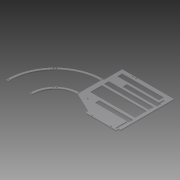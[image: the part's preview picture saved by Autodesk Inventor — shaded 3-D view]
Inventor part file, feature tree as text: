
AUTODESK INVENTOR PART (.ipt)
format: ipt  version: 2013 (Build 170138000, 138)  size: 532,992 bytes
history: native  units: in
note: dims shown in document units (in); Inventor stores cm internally (conversion verified against a paired STEP export)
features: extrude x17, sketch x17, reference x2
ambient origin geometry x8: Origin, YZ Plane, XZ Plane, XY Plane, X Axis, Y Axis, Z Axis, Center Point
feature tree (36):
  extrude  "Extrusion7"  Depth=1.0in
  extrude  "Extrusion8"  Depth=0.5in
  extrude  "Extrusion9"  Depth=5.25in
  extrude  "Extrusion10"  Depth=0.25in
  extrude  "Extrusion11"  Depth=7.625in
  extrude  "Extrusion13"  Depth=5.5in
  extrude  "Extrusion15"  Depth=12.125in
  extrude  "Extrusion16"  Depth=8.0in
  extrude  "Extrusion17"  Depth=2.75in
  extrude  "Extrusion18"  TaperAngle=90.0deg  [1 undecoded]
  extrude  "Extrusion19"  Depth=0.75in
  extrude  "Extrusion20"  Depth=10.5in
  extrude  "Extrusion21"  Depth=0.75in
  extrude  "Extrusion22"  Depth=10.5in
  extrude  "Extrusion23"  Depth=1.125in
  extrude  "Extrusion24"  Depth=0.5in
  extrude  "Extrusion25"  Depth=0.75in
  sketch  "Sketch1"  dims[d2=0.5in d3=0.5in d10=0.5in d11=0.5in d13=0.5in d14=0.266in d15=0.266in d16=0.266in d18=0.266in d20=0.25in d21=0.266in d22=0.266in d23=0.266in d26=0.266in d30=0.266in d32=0.266in d66=1.0in]
  sketch  "Sketch7"  dims[d67=0.0in d72=0.5in]
  sketch  "Sketch8"  dims[d81=4.25in d82=5.25in]
  sketch  "Sketch9"  dims[d83=11.0in d84=0.25in]
  sketch  "Sketch10"  dims[d85=12.5in d86=7.625in]
  sketch  "Sketch13"  dims[d87=2.1762in d88=5.5in]
  sketch  "Sketch14"  dims[d89=0.25in d90=0.0in d91=12.125in]
  reference  "Reference4"
  sketch  "Sketch16"  dims[d92=1.0in d93=8.0in]
  sketch  "Sketch17"  dims[d94=0.5in d95=2.75in]
  sketch  "Sketch18"  dims[d98=0.25in d99=0.0in d100=90.0deg]
  sketch  "Sketch19"  dims[d101=0.875in d102=0.75in]
  sketch  "Sketch20"  dims[d103=1.125in d104=10.5in]
  reference  "Reference9"
  sketch  "Sketch21"  dims[d105=1.125in d106=0.75in]
  sketch  "Sketch22"  dims[d107=0.5in d108=10.5in]
  sketch  "Sketch23"  dims[d109=1.125in d110=1.125in]
  sketch  "Sketch24"  dims[d111=0.5in d112=0.5in]
  sketch  "Sketch25"  dims[d113=10.5in d114=0.75in d115=0.75in d116=1.0in d117=0.0in d118=11.125in d119=0.25in d120=11.5in d121=1.0in d122=0.0in d123=0.5in d124=1.375in d125=135.0deg d126=0.25in d127=0.0in d135=1.0in d136=13.25in d137=0.5in d138=1.0in d139=0.0in d146=0.25in d148=0.25in d149=0.375in d150=1.0in d151=0.0in d153=0.25in d154=0.0in d155=0.5in d156=0.5in d157=0.25in d158=0.0in d159=1.25in d160=0.25in d161=0.0in d162=0.266in d164=0.25in d165=2.75in d166=1.0in d167=0.0in d168=1.0in d169=0.0in d170=0.266in d171=0.266in d172=1.125in d173=1.375in d174=1.125in d176=0.125in d177=1.0in d178=0.0in d179=0.875in d180=0.25in d181=0.0in d182=0.875in d183=0.25in d184=0.0in d185=0.25in d186=0.0in d187=1.0in d188=0.0in]
note: 1 required parameter value undecoded (feature->parameter linkage not recoverable at this tier; creation-order binding heuristic only, values carry confidence <= 0.55)
